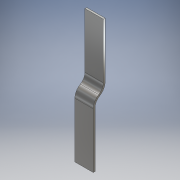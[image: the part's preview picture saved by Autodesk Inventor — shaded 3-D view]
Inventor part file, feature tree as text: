
AUTODESK INVENTOR PART (.ipt)
format: ipt  version: 2018 (Build 220112000, 112)  size: 109,056 bytes
history: native  units: mm
features: extrude x1, sketch x1
ambient origin geometry x8: Origin, YZ Plane, XZ Plane, XY Plane, X Axis, Y Axis, Z Axis, Center Point
bodies: Solid1 (feature_tree)
feature tree (2):
  extrude  "Extrusion1"  Depth=2.0mm
  sketch  "Sketch1"  dims[d0=0.2mm d1=6.0mm d2=6.0mm d3=1.1mm d4=1.0mm d5=2.0mm d6=0.0mm]
